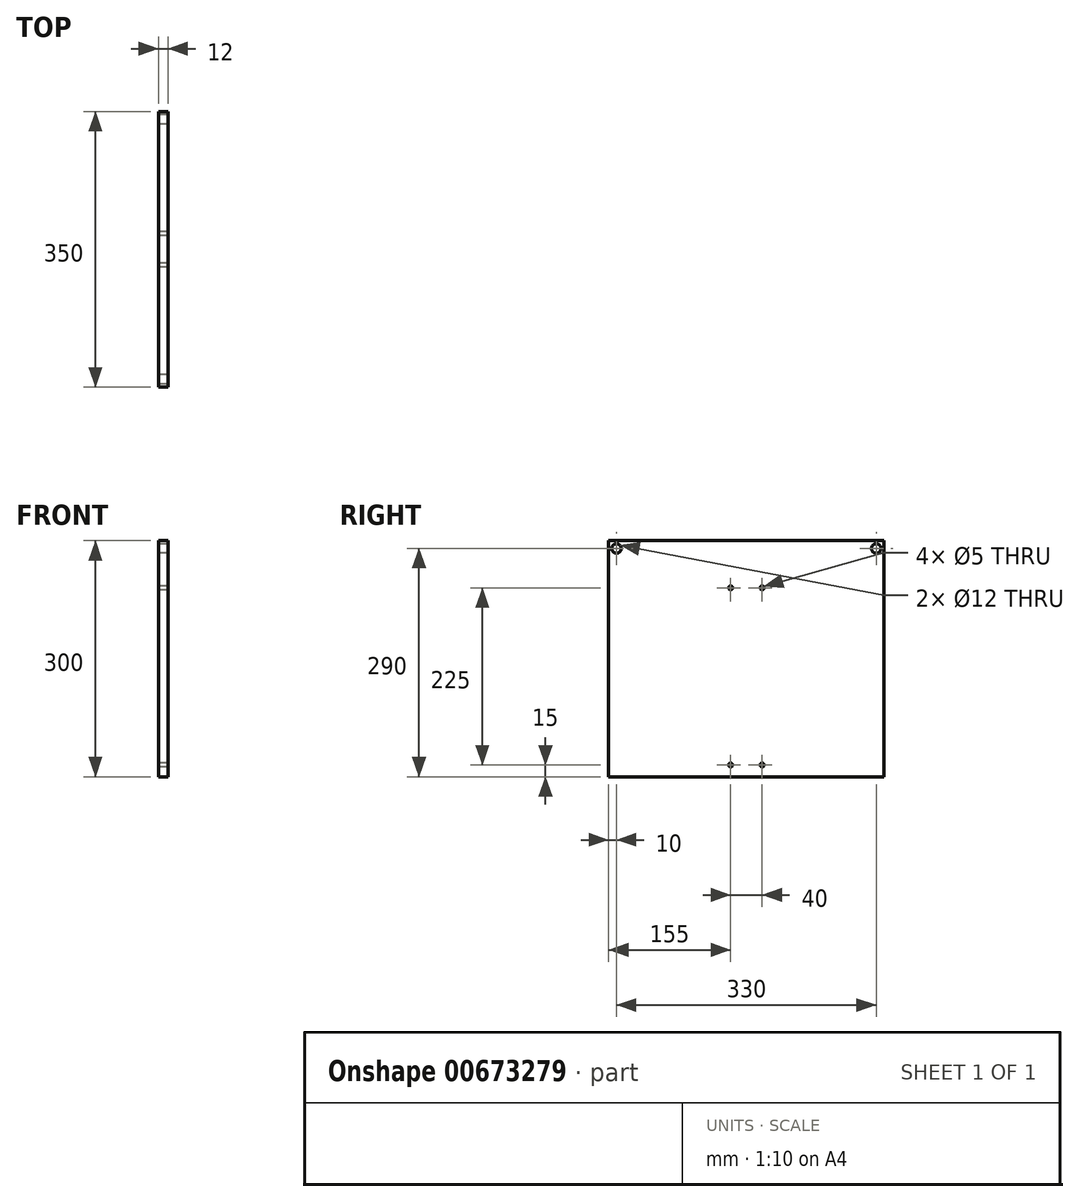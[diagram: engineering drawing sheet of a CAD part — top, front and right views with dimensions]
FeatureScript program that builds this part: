
annotation { "Feature Type Name" : "Feature", "Feature Type Description" : "" }
export const myFeature = defineFeature(function(context is Context, id is Id, definition is map)
    precondition{}
    {
        {
            var Q0;
            Q0=qCreatedBy(makeId("Right.planeOp"),FACE);
            var sketch = newSketch(context, id + "F0", { "sketchPlane" : qUnion([Q0])});
            skLineSegment(sketch, "E0", {"start": v(-175, 300) * mm, "end": v(175, 300) * mm});
            skLineSegment(sketch, "E1", {"start": v(175, 300) * mm, "end": v(175, 0) * mm});
            skLineSegment(sketch, "E2", {"start": v(175, 0) * mm, "end": v(-175, 0) * mm});
            skLineSegment(sketch, "E3", {"start": v(-175, 0) * mm, "end": v(-175, 300) * mm});
            skCircle(sketch, "E4", {"center": v(-165, 290) * mm, "radius": 6 * mm});
            skCircle(sketch, "E5", {"center": v(165, 290) * mm, "radius": 6 * mm});
            skLineSegment(sketch, "E6", {"start": v(0, 300) * mm, "end": v(0, 0) * mm, "construction": true});
            skCircle(sketch, "E7", {"center": v(-20, 240) * mm, "radius": 2.5 * mm});
            skCircle(sketch, "E8", {"center": v(20, 240) * mm, "radius": 2.5 * mm});
            skCircle(sketch, "E9", {"center": v(-20, 15) * mm, "radius": 2.5 * mm});
            skCircle(sketch, "E10", {"center": v(20, 15) * mm, "radius": 2.5 * mm});
            skSolve(sketch);
        }
        {
            var Q0;
            Q0=makeQuery(id+"F0.imprint","IMPRINT",FACE,{"disambiguationData":[TD([[makeQuery(id+"F0.imprint","IMPRINT",EDGE,{"derivedFrom":sQuery(id+"F0.wireOp",EDGE,"E0")}),-1.0]])]});
            extrude(context, id + "F1", {"entities" : qUnion([Q0]), "depth" : 12 * mm, "offsetDistance" : 25 * mm});
        }
    });
